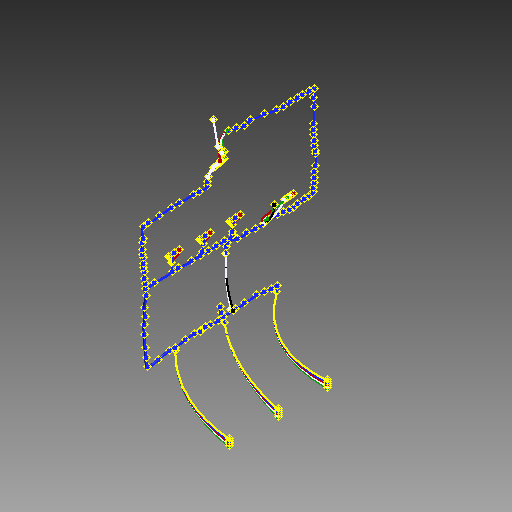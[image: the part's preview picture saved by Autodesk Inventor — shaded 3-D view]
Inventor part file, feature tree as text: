
AUTODESK INVENTOR PART (.ipt)
format: ipt  version: 2017 (Build 210142000, 142)  size: 1,136,640 bytes
history: native  units: mm (DEFAULTED — no unit token found)
features: other x205, plane x16, sketch x16, sweep x16
ambient origin geometry x8: Origin, YZ Plane, XZ Plane, XY Plane, X Axis, Y Axis, Z Axis, Center Point
bodies: Body1 (feature_tree), Body2 (feature_tree), Body3 (feature_tree), Body4 (feature_tree), Body5 (feature_tree), Body6 (feature_tree), Body7 (feature_tree), Body8 (feature_tree), Body9 (feature_tree), Body10 (feature_tree), Body11 (feature_tree), Body12 (feature_tree), Body13 (feature_tree), Body14 (feature_tree), Body15 (feature_tree), Body16 (feature_tree)
feature tree (253):
  other  "Work Point3"
  other  "Work Point4"
  other  "Wire1"
  other  "Work Point5"
  other  "Work Point6"
  other  "Wire2"
  other  "Work Point7"
  other  "Work Point8"
  other  "Wire3"
  other  "Work Point9"
  other  "Work Point10"
  other  "Wire4"
  other  "Work Point11"
  other  "Work Point12"
  other  "Wire5"
  other  "Work Point13"
  other  "Work Point14"
  other  "Wire6"
  other  "Work Point15"
  other  "Work Point16"
  other  "Wire7"
  other  "Work Point19"
  other  "Work Point20"
  other  "Wire9"
  other  "Work Point21"
  other  "Work Point22"
  other  "Wire8"
  other  "Work Point23"
  other  "Work Point24"
  other  "Wire10"
  other  "Work Point25"
  other  "Work Point26"
  other  "Wire11"
  other  "Work Point27"
  other  "Work Point28"
  other  "Wire12"
  other  "Work Point29"
  other  "Work Point30"
  other  "Wire13"
  other  "Work Point31"
  other  "Work Point32"
  other  "Wire14"
  other  "Work Point33"
  other  "Work Point34"
  other  "Wire15"
  other  "Work Point35"
  other  "Work Point36"
  other  "Wire16"
  other  "Work Point37"
  other  "Work Point38"
  other  "Wire17"
  other  "Work Point39"
  other  "Work Point40"
  other  "Wire18"
  other  "Work Point41"
  other  "Work Point42"
  other  "Wire19"
  other  "Work Point43"
  other  "Work Point44"
  other  "Wire20"
  other  "Work Point45"
  other  "Work Point46"
  other  "Wire21"
  other  "Work Point47"
  other  "Work Point48"
  other  "Wire22"
  other  "Work Point49"
  other  "Work Point50"
  other  "Segment1"
  other  "Work Point51"
  other  "Work Point52"
  other  "Work Point53"
  other  "Work Point54"
  other  "Work Point55"
  other  "Work Point56"
  other  "Work Point57"
  other  "Work Point58"
  other  "Work Point59"
  other  "Work Point60"
  other  "Work Point61"
  other  "Work Point62"
  other  "Work Point63"
  other  "Work Point64"
  other  "Work Point65"
  other  "Work Point66"
  other  "Segment2"
  other  "Work Point67"
  other  "Work Point68"
  other  "Work Point69"
  other  "Segment3"
  plane  "Work Plane2"
  other  "Segment4"
  plane  "Work Plane6"
  other  "Work Point70"
  other  "Segment5"
  other  "Work Point71"
  other  "Work Point72"
  other  "Work Point73"
  other  "Work Point74"
  other  "Work Point75"
  other  "Work Point76"
  other  "Work Point77"
  other  "Work Point78"
  other  "Work Point79"
  other  "Segment6"
  other  "Work Point80"
  other  "Work Point81"
  other  "Work Point82"
  other  "Work Point83"
  other  "Segment7"
  plane  "Work Plane8"
  plane  "Work Plane9"
  plane  "Work Plane10"
  other  "Segment8"
  plane  "Work Plane12"
  other  "Work Point84"
  other  "Segment9"
  other  "Work Point85"
  other  "Work Point86"
  other  "Work Point87"
  other  "Work Point88"
  other  "Work Point89"
  other  "Work Point90"
  plane  "Work Plane13"
  other  "Segment11"
  plane  "Work Plane14"
  plane  "Work Plane15"
  other  "Work Point103"
  other  "Work Point104"
  other  "Segment10"
  other  "Work Point105"
  other  "Work Point106"
  other  "Work Point107"
  other  "Work Point108"
  other  "Work Point109"
  other  "Work Point110"
  other  "Work Point111"
  other  "Work Point112"
  other  "Work Point113"
  other  "Work Point114"
  other  "Work Point115"
  other  "Work Point116"
  other  "Work Point117"
  other  "Work Point118"
  other  "Work Point119"
  other  "Work Point120"
  other  "Work Point121"
  other  "Work Point122"
  other  "Segment12"
  plane  "Work Plane17"
  plane  "Work Plane18"
  other  "Work Point124"
  other  "Work Point125"
  other  "Segment13"
  other  "Work Point126"
  other  "Work Point127"
  other  "Work Point128"
  other  "Work Point129"
  other  "Work Point130"
  other  "Work Point131"
  other  "Work Point132"
  other  "Work Point133"
  other  "Work Point134"
  other  "Work Point135"
  other  "Work Point136"
  other  "Work Point137"
  other  "Work Point138"
  other  "Work Point139"
  other  "Work Point140"
  other  "Work Point141"
  other  "Work Point142"
  other  "Work Point143"
  other  "Work Point144"
  other  "Work Point145"
  other  "Work Point146"
  other  "Work Point147"
  other  "Work Point148"
  other  "Work Point149"
  other  "Work Point150"
  other  "Work Point151"
  other  "Work Point152"
  other  "Work Point153"
  other  "Work Point154"
  other  "Work Point155"
  other  "Work Point156"
  other  "Work Point157"
  other  "Work Point158"
  plane  "Work Plane19"
  other  "Work Point159"
  other  "Work Point160"
  other  "Segment14"
  plane  "Work Plane20"
  other  "Work Point161"
  other  "Segment15"
  plane  "Work Plane21"
  plane  "Work Plane22"
  other  "Work Point162"
  other  "Work Point163"
  other  "Segment16"
  other  "Work Point164"
  other  "Work Point165"
  other  "Work Point166"
  other  "Work Point167"
  other  "Work Point168"
  plane  "Work Plane23"
  sketch  "Sketch2"  dims[d2=0.0mm d3=0.0mm d10=0.0mm d11=0.0mm]
  other  "Srf2"
  sketch  "Sketch6"  dims[d14=0.0mm d15=0.0mm d16=0.0mm d17=0.0mm]
  other  "Srf6"
  sketch  "Sketch8"  dims[d18=0.0mm d19=0.0mm d22=0.0mm d23=0.0mm]
  other  "Srf8"
  sketch  "Sketch9"  dims[d24=0.0mm d25=0.0mm d26=0.0mm d27=0.0mm]
  other  "Srf9"
  sketch  "Sketch10"  dims[d28=0.0mm d29=0.0mm d32=0.0mm d33=0.0mm]
  other  "Srf10"
  sketch  "Sketch12"  dims[d34=0.0mm d35=0.0mm d36=0.0mm d37=0.0mm]
  other  "Srf12"
  sketch  "Sketch13"  dims[d38=0.0mm d39=0.0mm d40=0.0mm d41=0.0mm]
  other  "Srf13"
  sketch  "Sketch14"  dims[d42=0.0mm d43=0.0mm d44=0.0mm d45=0.0mm]
  other  "Srf14"
  sketch  "Sketch15"
  other  "Srf15"
  sketch  "Sketch17"
  other  "Srf17"
  sketch  "Sketch18"
  other  "Srf18"
  sketch  "Sketch19"
  other  "Srf19"
  sketch  "Sketch20"
  other  "Srf20"
  sketch  "Sketch21"
  other  "Srf21"
  sketch  "Sketch22"
  other  "Srf22"
  sketch  "Sketch23"
  other  "Srf23"
  sweep  "SweepSrf2"
  sweep  "SweepSrf6"
  sweep  "SweepSrf8"
  sweep  "SweepSrf9"
  sweep  "SweepSrf10"
  sweep  "SweepSrf12"
  sweep  "SweepSrf13"
  sweep  "SweepSrf14"
  sweep  "SweepSrf15"
  sweep  "SweepSrf17"
  sweep  "SweepSrf18"
  sweep  "SweepSrf19"
  sweep  "SweepSrf20"
  sweep  "SweepSrf21"
  sweep  "SweepSrf22"
  sweep  "SweepSrf23"
